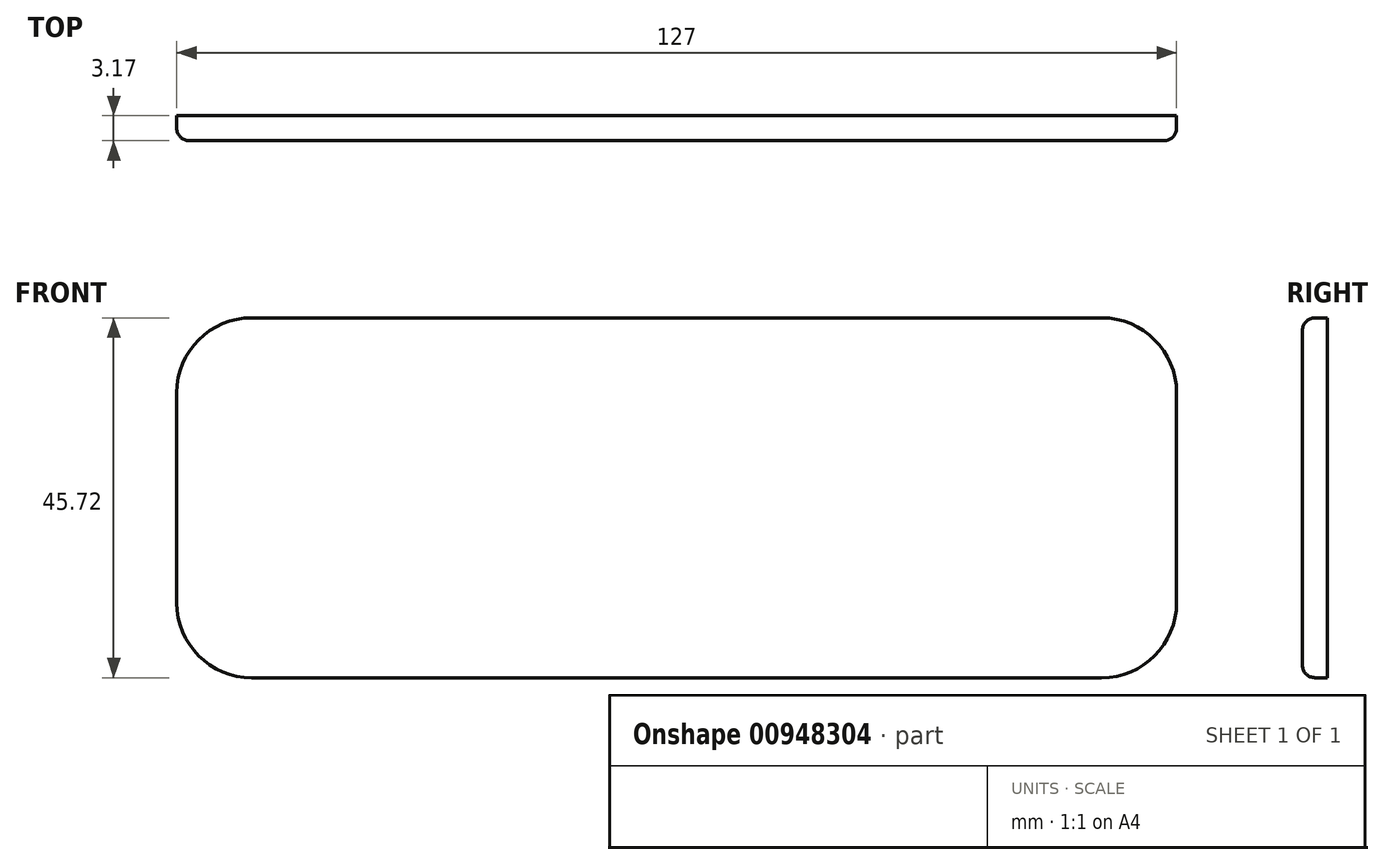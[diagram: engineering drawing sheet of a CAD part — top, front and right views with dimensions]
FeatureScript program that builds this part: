
annotation { "Feature Type Name" : "Feature", "Feature Type Description" : "" }
export const myFeature = defineFeature(function(context is Context, id is Id, definition is map)
    precondition{}
    {
        {
            var Q0;
            Q0=qCreatedBy(makeId("Front.planeOp"),FACE);
            var sketch = newSketch(context, id + "F0", { "sketchPlane" : qUnion([Q0])});
            skLineSegment(sketch, "E0.bottom", {"start": v(-53.98, 45.72) * mm, "end": v(53.98, 45.72) * mm});
            skLineSegment(sketch, "E0.top", {"start": v(-53.98, 0) * mm, "end": v(53.98, 0) * mm});
            skLineSegment(sketch, "E0.left", {"start": v(-63.5, 36.2) * mm, "end": v(-63.5, 9.52) * mm});
            skLineSegment(sketch, "E0.right", {"start": v(63.5, 36.2) * mm, "end": v(63.5, 9.53) * mm});
            skPoint(sketch, "E1.visualSharp", {"position": v(-63.5, 45.72) * mm});
            skArc(sketch, "E1.filletArc", {"start": v(-53.98, 45.72) * mm, "mid": v(-60.71, 42.93) * mm, "end": v(-63.5, 36.2) * mm});
            skPoint(sketch, "E2.visualSharp", {"position": v(-63.5, 0) * mm});
            skArc(sketch, "E2.filletArc", {"start": v(-63.5, 9.52) * mm, "mid": v(-60.71, 2.79) * mm, "end": v(-53.98, 0) * mm});
            skPoint(sketch, "E3.visualSharp", {"position": v(63.5, 0) * mm});
            skArc(sketch, "E3.filletArc", {"start": v(53.98, 0) * mm, "mid": v(60.71, 2.79) * mm, "end": v(63.5, 9.53) * mm});
            skPoint(sketch, "E4.visualSharp", {"position": v(63.5, 45.72) * mm});
            skArc(sketch, "E4.filletArc", {"start": v(63.5, 36.2) * mm, "mid": v(60.71, 42.93) * mm, "end": v(53.98, 45.72) * mm});
            skSolve(sketch);
        }
        {
            var Q0;
            Q0=makeQuery(id+"F0.imprint","IMPRINT",FACE,{"disambiguationData":[TD([[makeQuery(id+"F0.imprint","IMPRINT",EDGE,{"derivedFrom":sQuery(id+"F0.wireOp",EDGE,"E0.bottom")}),-1.0]])]});
            extrude(context, id + "F1", {"entities" : qUnion([Q0]), "depth" : 3.17 * mm, "offsetDistance" : 25.4 * mm});
        }
        {
            var Q0;
            Q0=makeQuery(id+"F1.opExtrude","CAP_FACE",FACE,{"disambiguationData":[OSD([sQuery(id+"F0.wireOp",EDGE,"E0.bottom"),sQuery(id+"F0.wireOp",EDGE,"E0.top"),sQuery(id+"F0.wireOp",EDGE,"E0.left"),sQuery(id+"F0.wireOp",EDGE,"E0.right"),sQuery(id+"F0.wireOp",EDGE,"E1.filletArc"),sQuery(id+"F0.wireOp",EDGE,"E2.filletArc"),sQuery(id+"F0.wireOp",EDGE,"E3.filletArc"),sQuery(id+"F0.wireOp",EDGE,"E4.filletArc")])],"isStart":false});
            var sketch = newSketch(context, id + "F2", { "sketchPlane" : qUnion([Q0])});
            skLineSegment(sketch, "E5", {"start": v(-63.41, 5.08) * mm, "end": v(63.5, 5.08) * mm});
            skLineSegment(sketch, "E6.bottom", {"start": v(-10.16, 40.64) * mm, "end": v(10.16, 40.64) * mm, "construction": true});
            skLineSegment(sketch, "E6.top", {"start": v(-10.16, 5.08) * mm, "end": v(10.16, 5.08) * mm, "construction": true});
            skLineSegment(sketch, "E6.left", {"start": v(-10.16, 40.64) * mm, "end": v(-10.16, 5.08) * mm, "construction": true});
            skLineSegment(sketch, "E6.right", {"start": v(10.16, 40.64) * mm, "end": v(10.16, 5.08) * mm, "construction": true});
            skLineSegment(sketch, "E7.bottom", {"start": v(13.97, 40.64) * mm, "end": v(34.3, 40.64) * mm, "construction": true});
            skLineSegment(sketch, "E7.top", {"start": v(13.97, 5.08) * mm, "end": v(34.3, 5.08) * mm, "construction": true});
            skLineSegment(sketch, "E7.left", {"start": v(13.97, 40.64) * mm, "end": v(13.97, 5.08) * mm, "construction": true});
            skLineSegment(sketch, "E7.right", {"start": v(34.3, 40.64) * mm, "end": v(34.3, 5.08) * mm, "construction": true});
            skLineSegment(sketch, "E8.bottom", {"start": v(38.1, 40.64) * mm, "end": v(58.42, 40.64) * mm, "construction": true});
            skLineSegment(sketch, "E8.top", {"start": v(38.1, 5.08) * mm, "end": v(58.42, 5.08) * mm, "construction": true});
            skLineSegment(sketch, "E8.left", {"start": v(38.1, 40.64) * mm, "end": v(38.1, 5.08) * mm, "construction": true});
            skLineSegment(sketch, "E8.right", {"start": v(58.42, 40.64) * mm, "end": v(58.42, 5.08) * mm, "construction": true});
            skLineSegment(sketch, "E9.bottom", {"start": v(-34.3, 40.64) * mm, "end": v(-13.97, 40.64) * mm, "construction": true});
            skLineSegment(sketch, "E9.top", {"start": v(-34.3, 5.08) * mm, "end": v(-13.97, 5.08) * mm, "construction": true});
            skLineSegment(sketch, "E9.left", {"start": v(-34.3, 40.64) * mm, "end": v(-34.3, 5.08) * mm, "construction": true});
            skLineSegment(sketch, "E9.right", {"start": v(-13.97, 40.64) * mm, "end": v(-13.97, 5.08) * mm, "construction": true});
            skLineSegment(sketch, "E10.bottom", {"start": v(-58.42, 40.64) * mm, "end": v(-38.1, 40.64) * mm, "construction": true});
            skLineSegment(sketch, "E10.top", {"start": v(-58.42, 5.08) * mm, "end": v(-38.1, 5.08) * mm, "construction": true});
            skLineSegment(sketch, "E10.left", {"start": v(-58.42, 40.64) * mm, "end": v(-58.42, 5.08) * mm, "construction": true});
            skLineSegment(sketch, "E10.right", {"start": v(-38.1, 40.64) * mm, "end": v(-38.1, 5.08) * mm, "construction": true});
            skLineSegment(sketch, "E11", {"start": v(-58.42, 22.86) * mm, "end": v(58.42, 22.86) * mm, "construction": true});
            skLineSegment(sketch, "E12", {"start": v(-48.26, 40.64) * mm, "end": v(-48.26, 5.08) * mm, "construction": true});
            skLineSegment(sketch, "E13", {"start": v(-24.13, 40.64) * mm, "end": v(-24.13, 5.08) * mm, "construction": true});
            skLineSegment(sketch, "E14", {"start": v(0, 40.64) * mm, "end": v(0, 5.08) * mm, "construction": true});
            skLineSegment(sketch, "E15", {"start": v(24.13, 40.64) * mm, "end": v(24.13, 5.08) * mm, "construction": true});
            skLineSegment(sketch, "E16", {"start": v(48.26, 40.64) * mm, "end": v(48.26, 5.08) * mm, "construction": true});
            skSolve(sketch);
        }
        {
            var Q0;
            Q0=makeQuery(id+"F1.opExtrude","CAP_FACE",FACE,{"disambiguationData":[OSD([sQuery(id+"F0.wireOp",EDGE,"E0.bottom"),sQuery(id+"F0.wireOp",EDGE,"E0.top"),sQuery(id+"F0.wireOp",EDGE,"E0.left"),sQuery(id+"F0.wireOp",EDGE,"E0.right"),sQuery(id+"F0.wireOp",EDGE,"E1.filletArc"),sQuery(id+"F0.wireOp",EDGE,"E2.filletArc"),sQuery(id+"F0.wireOp",EDGE,"E3.filletArc"),sQuery(id+"F0.wireOp",EDGE,"E4.filletArc")])],"isStart":false});
            fillet(context, id + "F3", {"entities" : qUnion([Q0]), "radius" : 1.59 * mm, "tangentPropagation" : true, "allowEdgeOverflow" : false});
        }
    });
